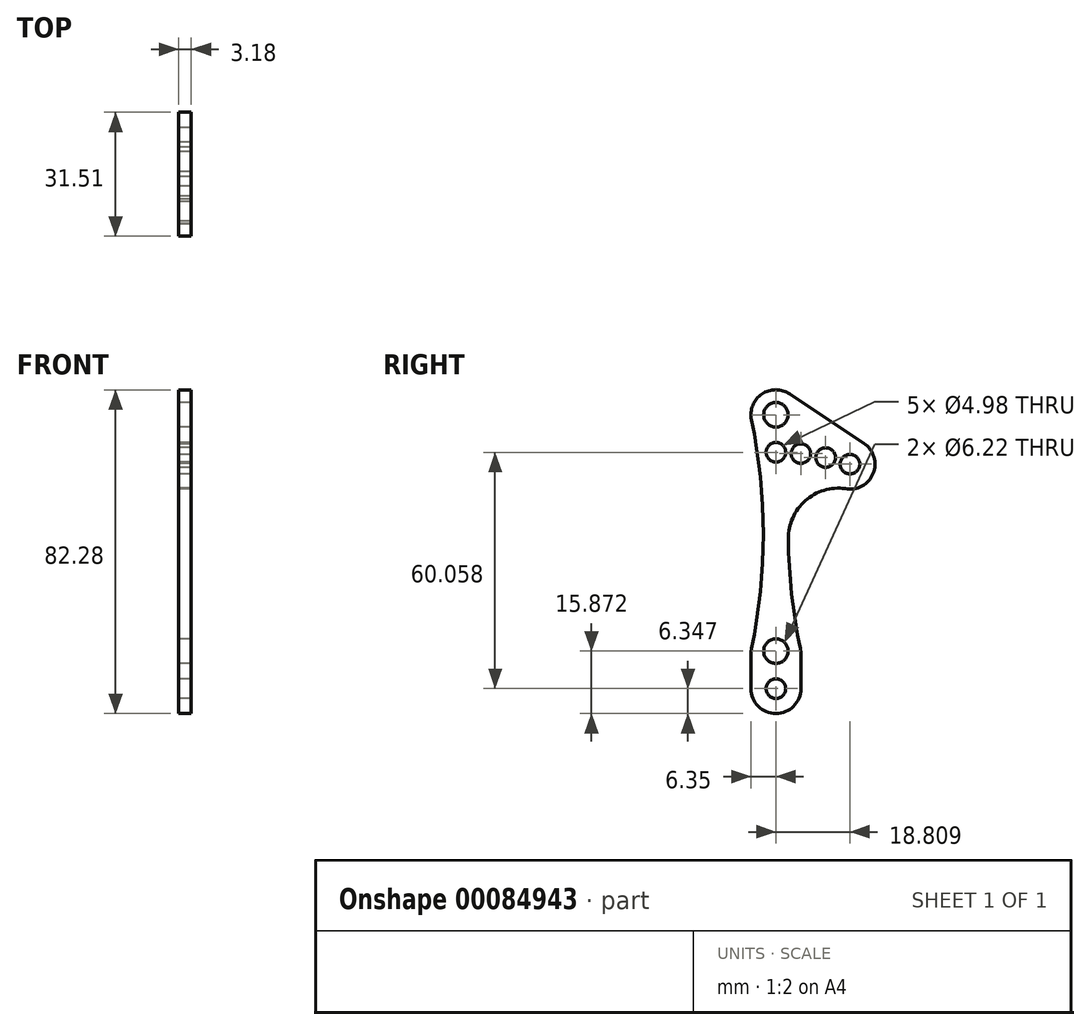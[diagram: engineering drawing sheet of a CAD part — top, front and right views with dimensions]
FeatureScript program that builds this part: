
annotation { "Feature Type Name" : "Feature", "Feature Type Description" : "" }
export const myFeature = defineFeature(function(context is Context, id is Id, definition is map)
    precondition{}
    {
        {
            var Q0;
            Q0=qCreatedBy(makeId("Right.planeOp"),FACE);
            var sketch = newSketch(context, id + "F0", { "sketchPlane" : qUnion([Q0])});
            skCircle(sketch, "E0", {"center": v(0, 0) * mm, "radius": 3.11 * mm});
            skCircle(sketch, "E1", {"center": v(0, -60.06) * mm, "radius": 3.11 * mm});
            skCircle(sketch, "E2", {"center": v(0, -9.53) * mm, "radius": 2.49 * mm});
            skCircle(sketch, "E3", {"center": v(0, -69.58) * mm, "radius": 2.49 * mm});
            skArc(sketch, "E4", {"start": v(3.52, 5.28) * mm, "mid": v(-3.56, 5.26) * mm, "end": v(-6.21, -1.3) * mm});
            skLineSegment(sketch, "E5", {"start": v(-6.35, -60.06) * mm, "end": v(-6.35, -60.06) * mm});
            skArc(sketch, "E6", {"start": v(3.17, -31.5) * mm, "mid": v(4, -45.53) * mm, "end": v(6.21, -59.42) * mm});
            skArc(sketch, "E7", {"start": v(-6.21, -59.42) * mm, "mid": v(-3.2, -30.36) * mm, "end": v(-6.21, -1.3) * mm});
            skArc(sketch, "E8", {"start": v(-6.35, -69.58) * mm, "mid": v(0, -75.93) * mm, "end": v(6.35, -69.58) * mm});
            skLineSegment(sketch, "E9", {"start": v(6.35, -60.73) * mm, "end": v(6.35, -69.58) * mm});
            skLineSegment(sketch, "E10", {"start": v(-6.35, -60.73) * mm, "end": v(-6.35, -69.58) * mm});
            skPoint(sketch, "E11.visualSharp", {"position": v(6.35, -60.06) * mm});
            skArc(sketch, "E11.filletArc", {"start": v(6.35, -60.73) * mm, "mid": v(6.32, -60.07) * mm, "end": v(6.21, -59.42) * mm});
            skPoint(sketch, "E12.visualSharp", {"position": v(-6.35, -60.06) * mm});
            skArc(sketch, "E12.filletArc", {"start": v(-6.21, -59.42) * mm, "mid": v(-6.32, -60.07) * mm, "end": v(-6.35, -60.73) * mm});
            skPoint(sketch, "E13.visualSharp", {"position": v(6.35, 0) * mm});
            skLineSegment(sketch, "E14.filletArc", {"start": v(-6.21, -1.3) * mm, "end": v(-6.21, -1.3) * mm});
            skLineSegment(sketch, "E15.bottom", {"start": v(-7.94, -79.24) * mm, "end": v(7.94, -79.24) * mm, "construction": true});
            skLineSegment(sketch, "E15.top", {"start": v(-7.94, 9.66) * mm, "end": v(7.94, 9.66) * mm, "construction": true});
            skLineSegment(sketch, "E15.left", {"start": v(-7.94, -79.24) * mm, "end": v(-7.94, 9.66) * mm, "construction": true});
            skLineSegment(sketch, "E16", {"start": v(0, -75.93) * mm, "end": v(0, 6.35) * mm, "construction": true});
            skPoint(sketch, "E16.startSnap0", {"position": v(0, -75.93) * mm});
            skPoint(sketch, "E17", {"position": v(0, -34.8) * mm});
            skCircle(sketch, "E18", {"center": v(12.63, -10.87) * mm, "radius": 2.49 * mm});
            skCircle(sketch, "E19", {"center": v(18.8, -12.55) * mm, "radius": 2.49 * mm});
            skCircle(sketch, "E20", {"center": v(0, -69.58) * mm, "radius": 60.06 * mm, "construction": true});
            skArc(sketch, "E21", {"start": v(17.63, -18.79) * mm, "mid": v(24.69, -14.95) * mm, "end": v(22.33, -7.26) * mm});
            skArc(sketch, "E22", {"start": v(17.63, -18.79) * mm, "mid": v(7.48, -21.82) * mm, "end": v(3.17, -31.5) * mm});
            skLineSegment(sketch, "E23", {"start": v(3.52, 5.28) * mm, "end": v(22.33, -7.26) * mm});
            skCircle(sketch, "E24", {"center": v(6.34, -9.86) * mm, "radius": 2.49 * mm});
            skPoint(sketch, "E25.end.orphan", {"position": v(-6.35, 0) * mm});
            skSolve(sketch);
        }
        {
            var Q0;
            {var subQ0=sQuery(id+"F0.wireOp",EDGE,"E10");var subQ1=sQuery(id+"F0.wireOp",EDGE,"E8");var subQ2=makeQuery(id+"F0.imprint","INTERSECT",VERTEX,{"disambiguationData":[OD(0.0)],"derivedFrom":[subQ1,subQ0]});Q0=makeQuery(id+"F0.imprint","IMPRINT",FACE,{"disambiguationData":[TD([[makeQuery(id+"F0.imprint","IMPRINT",EDGE,{"disambiguationData":[TD([[subQ2,-1.0]])],"derivedFrom":subQ1}),1.0]])]});}
            var Q1;
            Q1=makeQuery(id+"F0.imprint","IMPRINT",FACE,{"disambiguationData":[TD([[makeQuery(id+"F0.imprint","IMPRINT",EDGE,{"derivedFrom":sQuery(id+"F0.wireOp",EDGE,"E0")}),-1.0]])]});
            extrude(context, id + "F1", {"entities" : qUnion([Q0, Q1]), "depth" : 3.17 * mm});
        }
    });
